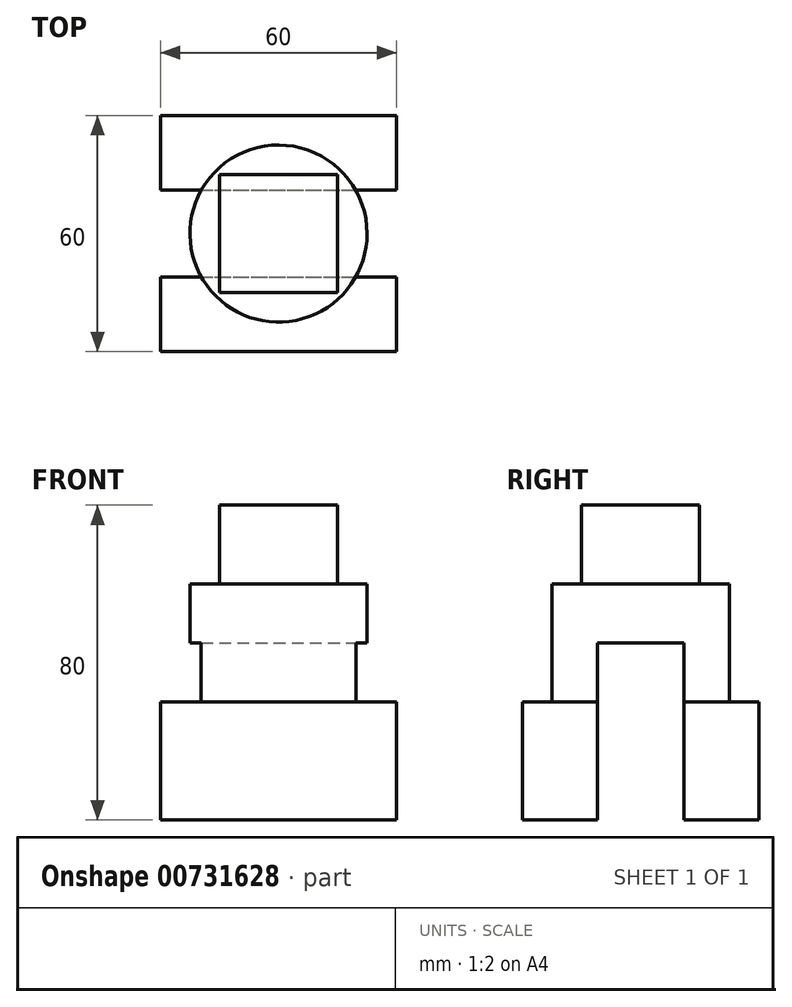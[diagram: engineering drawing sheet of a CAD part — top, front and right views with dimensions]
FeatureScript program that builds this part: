
annotation { "Feature Type Name" : "Feature", "Feature Type Description" : "" }
export const myFeature = defineFeature(function(context is Context, id is Id, definition is map)
    precondition{}
    {
        {
            var Q0;
            Q0=qCreatedBy(makeId("Top.planeOp"),FACE);
            var sketch = newSketch(context, id + "F0", { "sketchPlane" : qUnion([Q0])});
            skLineSegment(sketch, "E0.bottom", {"start": v(-30, 30) * mm, "end": v(30, 30) * mm});
            skLineSegment(sketch, "E0.top", {"start": v(-30, -30) * mm, "end": v(30, -30) * mm});
            skLineSegment(sketch, "E0.left", {"start": v(-30, 30) * mm, "end": v(-30, -30) * mm});
            skLineSegment(sketch, "E0.right", {"start": v(30, 30) * mm, "end": v(30, -30) * mm});
            skSolve(sketch);
        }
        {
            var Q0;
            Q0=makeQuery(id+"F0.imprint","IMPRINT",FACE,{"disambiguationData":[TD([[makeQuery(id+"F0.imprint","IMPRINT",EDGE,{"derivedFrom":sQuery(id+"F0.wireOp",EDGE,"E0.bottom")}),-1.0]])]});
            extrude(context, id + "F1", {"entities" : qUnion([Q0]), "depth" : 30 * mm, "offsetDistance" : 25 * mm});
        }
        {
            var Q0;
            Q0=makeQuery(id+"F1.opExtrude","CAP_FACE",FACE,{"disambiguationData":[OSD([sQuery(id+"F0.wireOp",EDGE,"E0.bottom"),sQuery(id+"F0.wireOp",EDGE,"E0.top"),sQuery(id+"F0.wireOp",EDGE,"E0.left"),sQuery(id+"F0.wireOp",EDGE,"E0.right")])],"isStart":false});
            var sketch = newSketch(context, id + "F2", { "sketchPlane" : qUnion([Q0])});
            skCircle(sketch, "E1", {"center": v(0, 0) * mm, "radius": 22.5 * mm});
            skSolve(sketch);
        }
        {
            var Q0;
            Q0=makeQuery(id+"F2.imprint","IMPRINT",FACE,{"disambiguationData":[TD([[makeQuery(id+"F2.imprint","IMPRINT",EDGE,{"derivedFrom":sQuery(id+"F2.wireOp",EDGE,"E1")}),1.0]])]});
            extrude(context, id + "F3", {"entities" : qUnion([Q0]), "operationType" : NewBodyOperationType.ADD, "depth" : 30 * mm, "offsetDistance" : 25 * mm});
        }
        {
            var Q0;
            Q0=makeQuery(id+"F3.opExtrude","CAP_FACE",FACE,{"disambiguationData":[OSD([sQuery(id+"F2.wireOp",EDGE,"E1")])],"isStart":false});
            var sketch = newSketch(context, id + "F4", { "sketchPlane" : qUnion([Q0])});
            skLineSegment(sketch, "E2.bottom", {"start": v(-15, 15) * mm, "end": v(15, 15) * mm});
            skLineSegment(sketch, "E2.top", {"start": v(-15, -15) * mm, "end": v(15, -15) * mm});
            skLineSegment(sketch, "E2.left", {"start": v(-15, 15) * mm, "end": v(-15, -15) * mm});
            skLineSegment(sketch, "E2.right", {"start": v(15, 15) * mm, "end": v(15, -15) * mm});
            skSolve(sketch);
        }
        {
            var Q0;
            Q0=makeQuery(id+"F4.imprint","IMPRINT",FACE,{"disambiguationData":[TD([[makeQuery(id+"F4.imprint","IMPRINT",EDGE,{"derivedFrom":sQuery(id+"F4.wireOp",EDGE,"E2.bottom")}),-1.0]])]});
            extrude(context, id + "F5", {"entities" : qUnion([Q0]), "operationType" : NewBodyOperationType.ADD, "depth" : 20 * mm, "offsetDistance" : 25 * mm});
        }
        {
            var Q0;
            Q0=makeQuery(id+"F1.opExtrude","SWEPT_FACE",FACE,{"disambiguationData":[OSD([sQuery(id+"F0.wireOp",EDGE,"E0.right")])]});
            var sketch = newSketch(context, id + "F6", { "sketchPlane" : qUnion([Q0])});
            skLineSegment(sketch, "E3.bottom", {"start": v(-11, 45) * mm, "end": v(11, 45) * mm});
            skLineSegment(sketch, "E3.top", {"start": v(-11, 0) * mm, "end": v(11, 0) * mm});
            skLineSegment(sketch, "E3.left", {"start": v(-11, 45) * mm, "end": v(-11, 0) * mm});
            skLineSegment(sketch, "E3.right", {"start": v(11, 45) * mm, "end": v(11, 0) * mm});
            skSolve(sketch);
        }
        {
            var Q0;
            Q0 = qSketchRegion(id + "F6", true);
            extrude(context, id + "F7", {"entities" : qUnion([Q0]), "operationType" : NewBodyOperationType.REMOVE, "oppositeDirection" : true, "depth" : 60 * mm, "offsetDistance" : 25 * mm});
        }
    });
